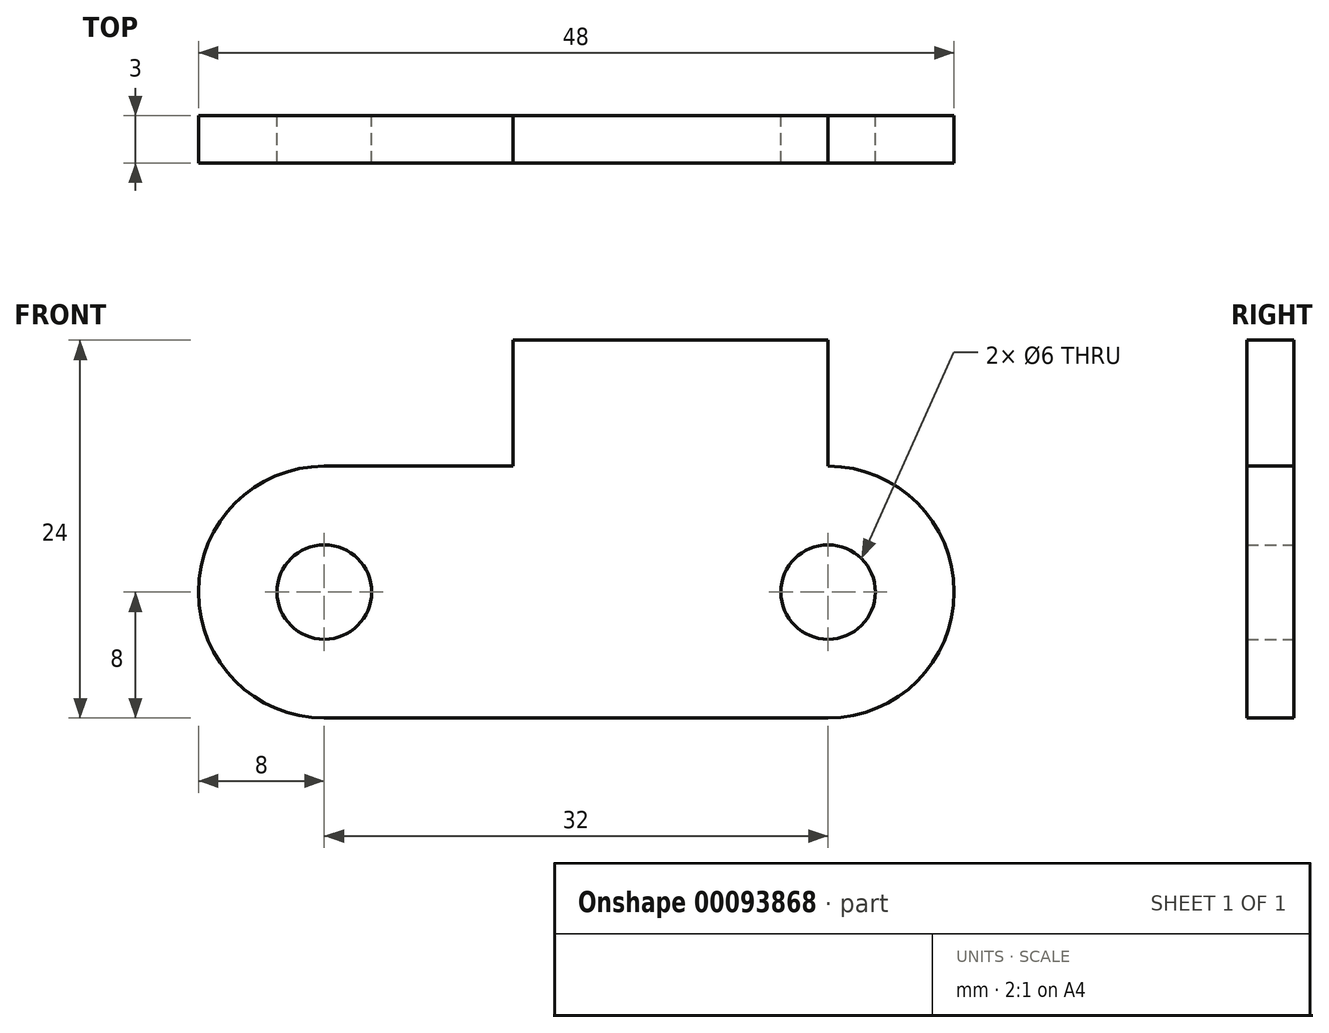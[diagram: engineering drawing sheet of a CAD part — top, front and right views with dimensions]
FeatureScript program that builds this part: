
annotation { "Feature Type Name" : "Feature", "Feature Type Description" : "" }
export const myFeature = defineFeature(function(context is Context, id is Id, definition is map)
    precondition{}
    {
        {
            var Q0;
            Q0=qCreatedBy(makeId("Front.planeOp"),FACE);
            var sketch = newSketch(context, id + "F0", { "sketchPlane" : qUnion([Q0])});
            skLineSegment(sketch, "E0", {"start": v(-16, 0) * mm, "end": v(16, 0) * mm});
            skCircle(sketch, "E1", {"center": v(-16, 0) * mm, "radius": 3 * mm});
            skCircle(sketch, "E2", {"center": v(16, 0) * mm, "radius": 3 * mm});
            skArc(sketch, "E3.0.startCap", {"start": v(-16, -8) * mm, "mid": v(-24, 0) * mm, "end": v(-16, 8) * mm});
            skArc(sketch, "E3.0.endCap", {"start": v(16, 8) * mm, "mid": v(24, 0) * mm, "end": v(16, -8) * mm});
            skLineSegment(sketch, "E3.0.left", {"start": v(-16, 8) * mm, "end": v(-4, 8) * mm});
            skLineSegment(sketch, "E3.0.right", {"start": v(-16, -8) * mm, "end": v(16, -8) * mm});
            skLineSegment(sketch, "E4", {"start": v(16, 0) * mm, "end": v(16, 16) * mm});
            skLineSegment(sketch, "E5", {"start": v(16, 16) * mm, "end": v(-4, 16) * mm});
            skLineSegment(sketch, "E6", {"start": v(-4, 16) * mm, "end": v(-4, 8) * mm});
            skPoint(sketch, "E7.endSnap0", {"position": v(-4, 12) * mm});
            skSolve(sketch);
        }
        {
            var Q0;
            Q0 = qSketchRegion(id + "F0", true);
            extrude(context, id + "F1", {"entities" : qUnion([Q0]), "depth" : 3 * mm});
        }
    });
